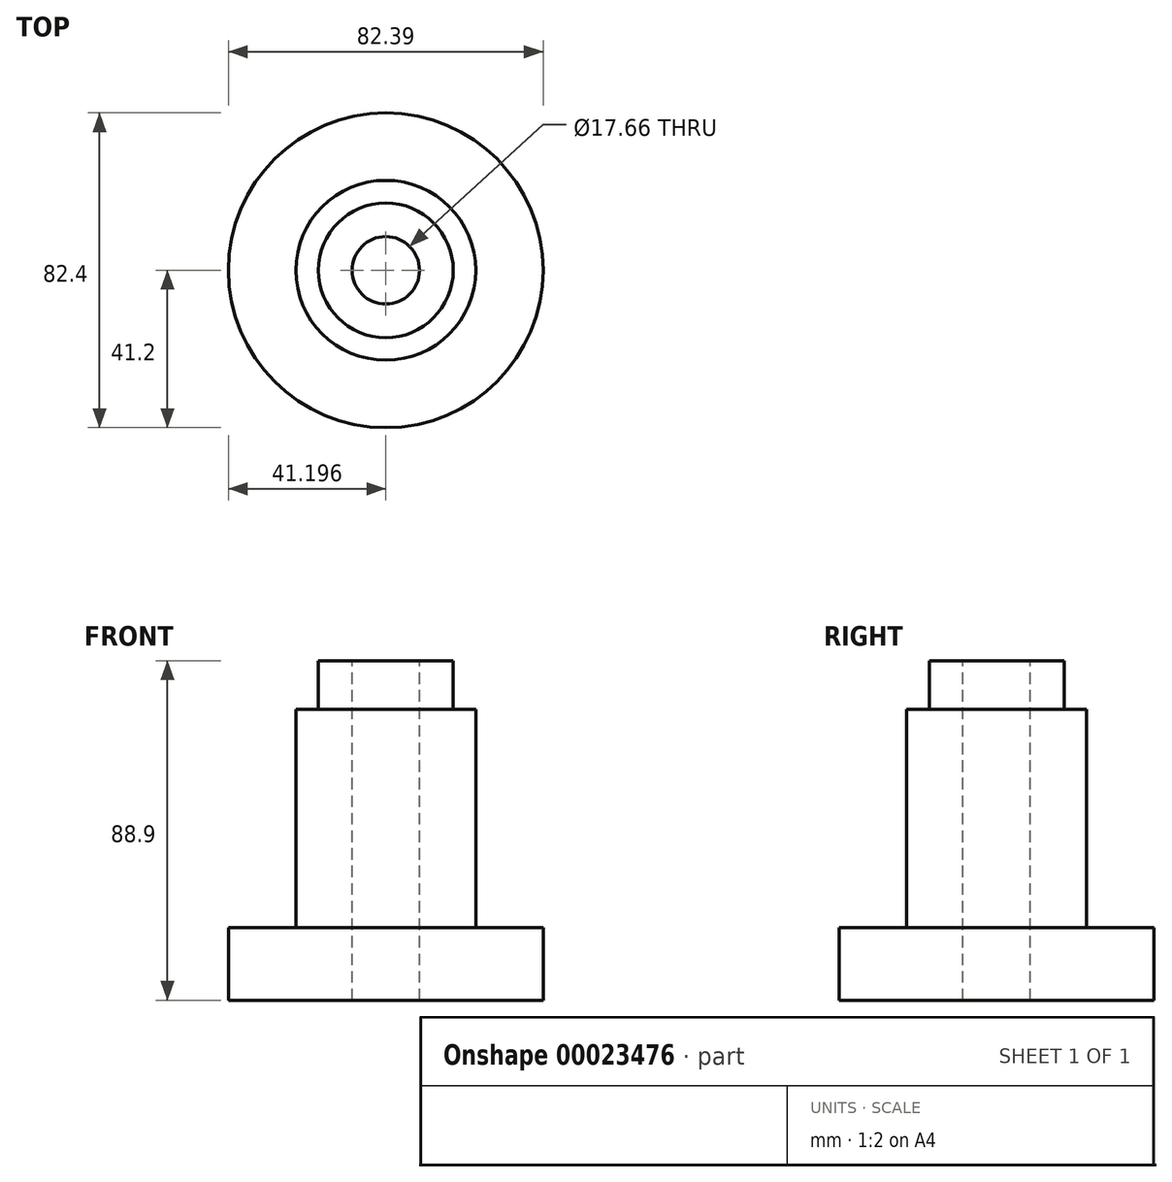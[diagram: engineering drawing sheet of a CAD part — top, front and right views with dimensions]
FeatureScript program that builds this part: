
annotation { "Feature Type Name" : "Feature", "Feature Type Description" : "" }
export const myFeature = defineFeature(function(context is Context, id is Id, definition is map)
    precondition{}
    {
        {
            var Q0;
            Q0=qCreatedBy(makeId("Front.planeOp"),FACE);
            var sketch = newSketch(context, id + "F0", { "sketchPlane" : qUnion([Q0])});
            skLineSegment(sketch, "E0", {"start": v(-16.62, 48.22) * mm, "end": v(-16.62, -40.68) * mm, "construction": true});
            skLineSegment(sketch, "E1.bottom", {"start": v(-7.8, 48.22) * mm, "end": v(1.03, 48.22) * mm});
            skLineSegment(sketch, "E1.top", {"start": v(-7.8, 35.52) * mm, "end": v(1.03, 35.52) * mm});
            skLineSegment(sketch, "E1.left", {"start": v(-7.8, 48.22) * mm, "end": v(-7.8, 35.52) * mm});
            skLineSegment(sketch, "E1.right", {"start": v(1.03, 48.22) * mm, "end": v(1.03, 35.52) * mm});
            skLineSegment(sketch, "E2.bottom", {"start": v(-7.8, 35.52) * mm, "end": v(6.92, 35.52) * mm});
            skLineSegment(sketch, "E2.top", {"start": v(-7.8, -21.63) * mm, "end": v(6.92, -21.63) * mm});
            skLineSegment(sketch, "E2.left", {"start": v(-7.8, 35.52) * mm, "end": v(-7.8, -21.63) * mm});
            skLineSegment(sketch, "E2.right", {"start": v(6.92, 35.52) * mm, "end": v(6.92, -21.63) * mm});
            skLineSegment(sketch, "E3.bottom", {"start": v(-7.8, -21.63) * mm, "end": v(24.57, -21.63) * mm});
            skLineSegment(sketch, "E3.top", {"start": v(-7.8, -40.68) * mm, "end": v(24.57, -40.68) * mm});
            skLineSegment(sketch, "E3.left", {"start": v(-7.8, -21.63) * mm, "end": v(-7.8, -40.68) * mm});
            skLineSegment(sketch, "E3.right", {"start": v(24.57, -21.63) * mm, "end": v(24.57, -40.68) * mm});
            skSolve(sketch);
        }
        {
            var Q0;
            Q0=makeQuery(id+"F0.imprint","IMPRINT",FACE,{"disambiguationData":[TD([[makeQuery(id+"F0.imprint","IMPRINT",EDGE,{"derivedFrom":sQuery(id+"F0.wireOp",EDGE,"E1.bottom")}),-1.0]])]});
            var Q1;
            {var subQ2=sQuery(id+"F0.wireOp",EDGE,"E2.left");Q1=makeQuery(id+"F0.imprint","IMPRINT",FACE,{"disambiguationData":[TD([[makeQuery(id+"F0.imprint","IMPRINT",EDGE,{"derivedFrom":subQ2}),1.0]])]});}
            var Q2;
            Q2=makeQuery(id+"F0.imprint","IMPRINT",FACE,{"disambiguationData":[TD([[makeQuery(id+"F0.imprint","IMPRINT",EDGE,{"derivedFrom":sQuery(id+"F0.wireOp",EDGE,"E3.top")}),1.0]])]});
            var Q3;
            Q3=sQuery(id+"F0.wireOp",EDGE,"E0");
            revolve(context, id + "F1", {"entities" : qUnion([Q0, Q1, Q2]), "axis" : qUnion([Q3]), "revolveType" : RevolveType.FULL});
        }
    });
